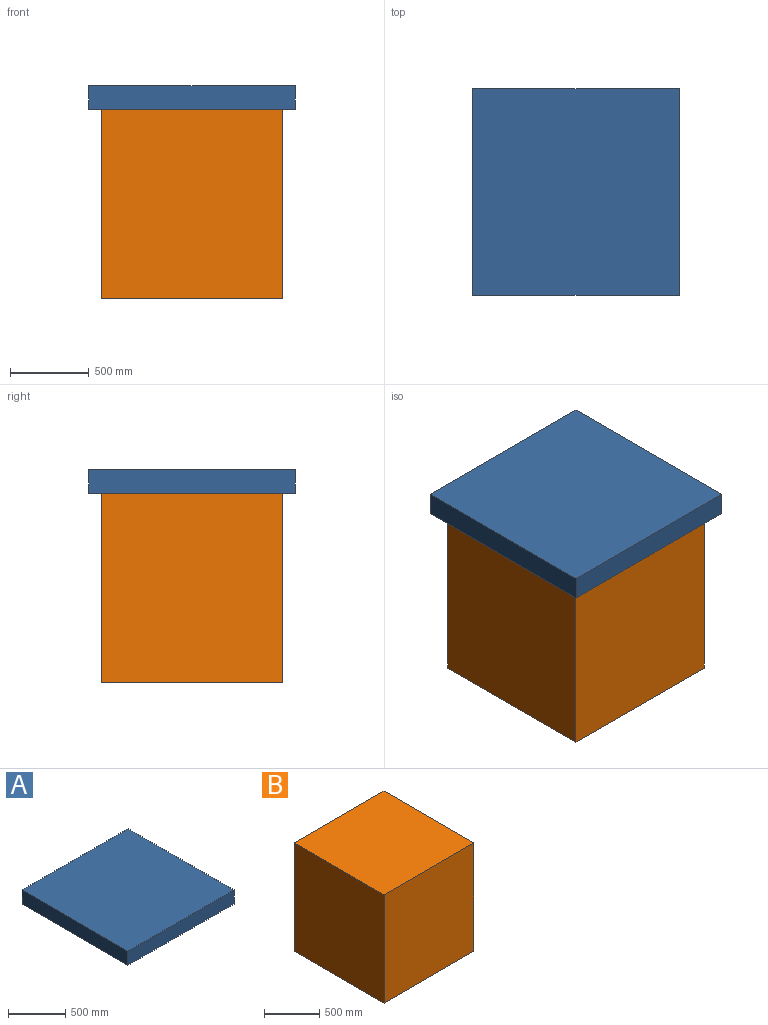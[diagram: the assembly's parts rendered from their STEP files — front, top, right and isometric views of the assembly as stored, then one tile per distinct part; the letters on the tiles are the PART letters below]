
ASSEMBLY  parts=2 mates=1
PART A: 6 faces, bbox 1310x1310x150 mm
  f0: plane 1310x150mm, normal (0,-1,0), area 196500mm2, adj f1,f3,f4,f5
  f1: plane 1310x150mm, normal (1,0,0), area 196500mm2, adj f0,f2,f4,f5
  f2: plane 1310x150mm, normal (0,1,0), area 196500mm2, adj f1,f3,f4,f5
  f3: plane 1310x150mm, normal (-1,0,0), area 196500mm2, adj f0,f2,f4,f5
  f4: plane 1310x1310mm, normal (0,0,1), area 1716100mm2, adj f0,f1,f2,f3
  f5: plane 1310x1310mm, normal (0,0,-1), area 1716100mm2, adj f0,f1,f2,f3
PART B: 6 faces, bbox 1150x1150x1200 mm
  f0: plane 1200x1150mm, normal (0,-1,0), area 1380000mm2, adj f1,f3,f4,f5
  f1: plane 1200x1150mm, normal (1,0,0), area 1380000mm2, adj f0,f2,f4,f5
  f2: plane 1200x1150mm, normal (0,1,0), area 1380000mm2, adj f1,f3,f4,f5
  f3: plane 1200x1150mm, normal (-1,0,0), area 1380000mm2, adj f0,f2,f4,f5
  f4: plane 1150x1150mm, normal (0,0,1), area 1322500mm2, adj f0,f1,f2,f3
  f5: plane 1150x1150mm, normal (0,0,-1), area 1322500mm2, adj f0,f1,f2,f3
PLACE A t=(98.08,256.07,899.17)mm
PLACE B t=(98.08,256.07,-300.83)mm
MATE parallel A.f5 <-> B.f4  axis (0,0,-1) through (98.08,256.07,899.17)mm
